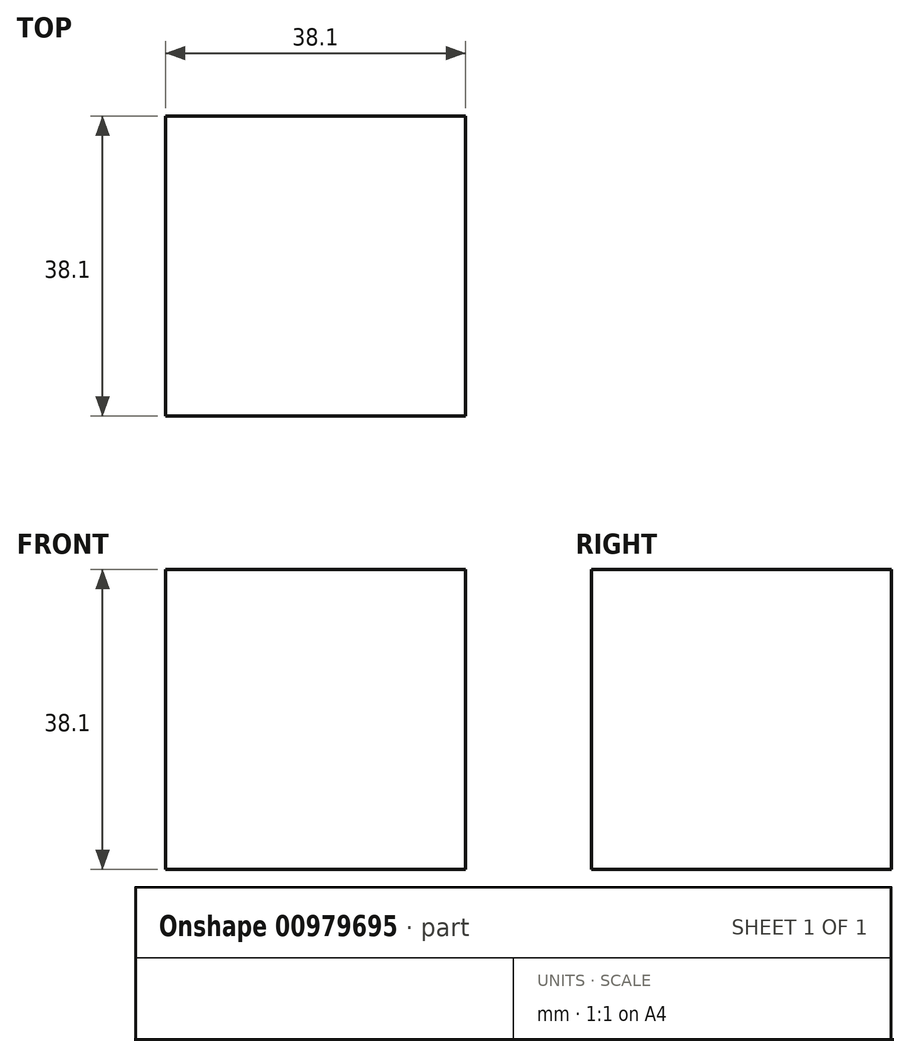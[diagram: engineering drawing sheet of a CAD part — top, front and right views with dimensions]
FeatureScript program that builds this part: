
annotation { "Feature Type Name" : "Feature", "Feature Type Description" : "" }
export const myFeature = defineFeature(function(context is Context, id is Id, definition is map)
    precondition{}
    {
        {
            var Q0;
            Q0=qCreatedBy(makeId("Front.planeOp"),FACE);
            var sketch = newSketch(context, id + "F0", { "sketchPlane" : qUnion([Q0])});
            skLineSegment(sketch, "E0.bottom", {"start": v(0, 0) * mm, "end": v(38.1, 0) * mm});
            skLineSegment(sketch, "E0.top", {"start": v(0, 38.1) * mm, "end": v(38.1, 38.1) * mm});
            skLineSegment(sketch, "E0.left", {"start": v(0, 0) * mm, "end": v(0, 38.1) * mm});
            skLineSegment(sketch, "E0.right", {"start": v(38.1, 0) * mm, "end": v(38.1, 38.1) * mm});
            skSolve(sketch);
        }
        {
            var Q0;
            Q0 = qSketchRegion(id + "F0", true);
            extrude(context, id + "F1", {"entities" : qUnion([Q0]), "depth" : 38.1 * mm, "offsetDistance" : 25.4 * mm});
        }
    });
